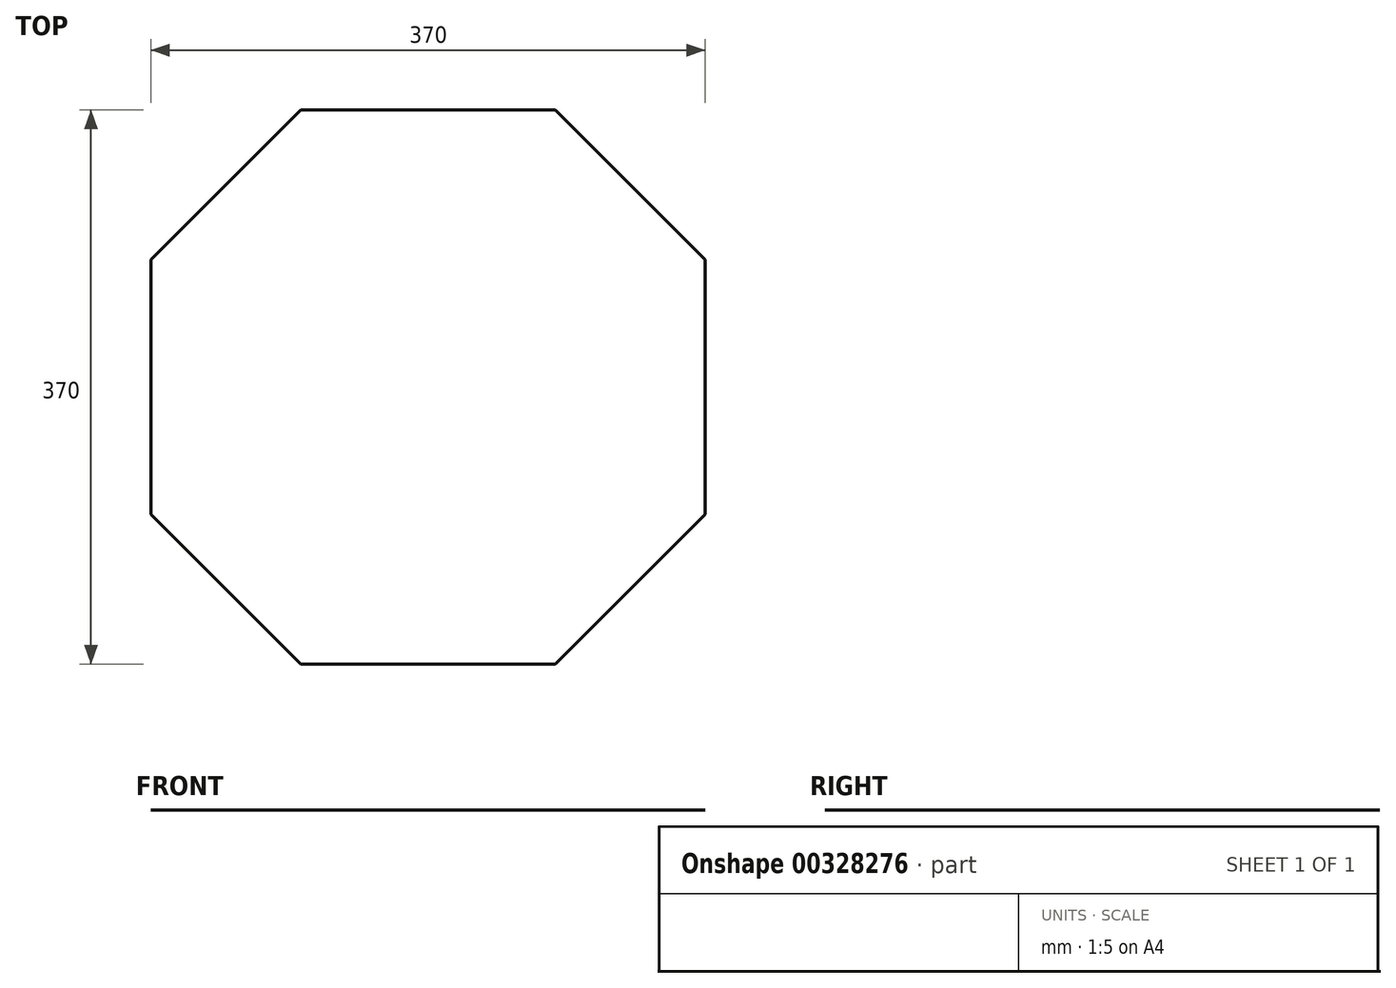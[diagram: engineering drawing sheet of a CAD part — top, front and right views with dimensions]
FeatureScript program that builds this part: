
annotation { "Feature Type Name" : "Feature", "Feature Type Description" : "" }
export const myFeature = defineFeature(function(context is Context, id is Id, definition is map)
    precondition{}
    {
        {
            var Q0;
            Q0=qCreatedBy(makeId("Top.planeOp"),FACE);
            var sketch = newSketch(context, id + "F0", { "sketchPlane" : qUnion([Q0])});
            skLineSegment(sketch, "E0.bottom", {"start": v(85, -185) * mm, "end": v(-85, -185) * mm});
            skLineSegment(sketch, "E0.top", {"start": v(85, 185) * mm, "end": v(-85, 185) * mm});
            skLineSegment(sketch, "E0.left", {"start": v(185, -85) * mm, "end": v(185, 85) * mm});
            skLineSegment(sketch, "E0.right", {"start": v(-185, -85) * mm, "end": v(-185, 85) * mm});
            skPoint(sketch, "E0.middle", {"position": v(0, 0) * mm});
            skLineSegment(sketch, "E1", {"start": v(-185, -85) * mm, "end": v(-85, -185) * mm});
            skPoint(sketch, "E2.orphan", {"position": v(-185, -185) * mm});
            skLineSegment(sketch, "E3", {"start": v(-185, 85) * mm, "end": v(-85, 185) * mm});
            skPoint(sketch, "E4.orphan", {"position": v(-185, 185) * mm});
            skLineSegment(sketch, "E5", {"start": v(85, 185) * mm, "end": v(185, 85) * mm});
            skLineSegment(sketch, "E6", {"start": v(185, -85) * mm, "end": v(85, -185) * mm});
            skPoint(sketch, "E7.orphan", {"position": v(185, -185) * mm});
            skPoint(sketch, "E8.orphan", {"position": v(185, 185) * mm});
            skSolve(sketch);
        }
        {
            var Q0;
            Q0 = qSketchRegion(id + "F0", true);
            extrude(context, id + "F1", {"entities" : qUnion([Q0]), "depth" : 1 / 203.2 * mm});
        }
    });
